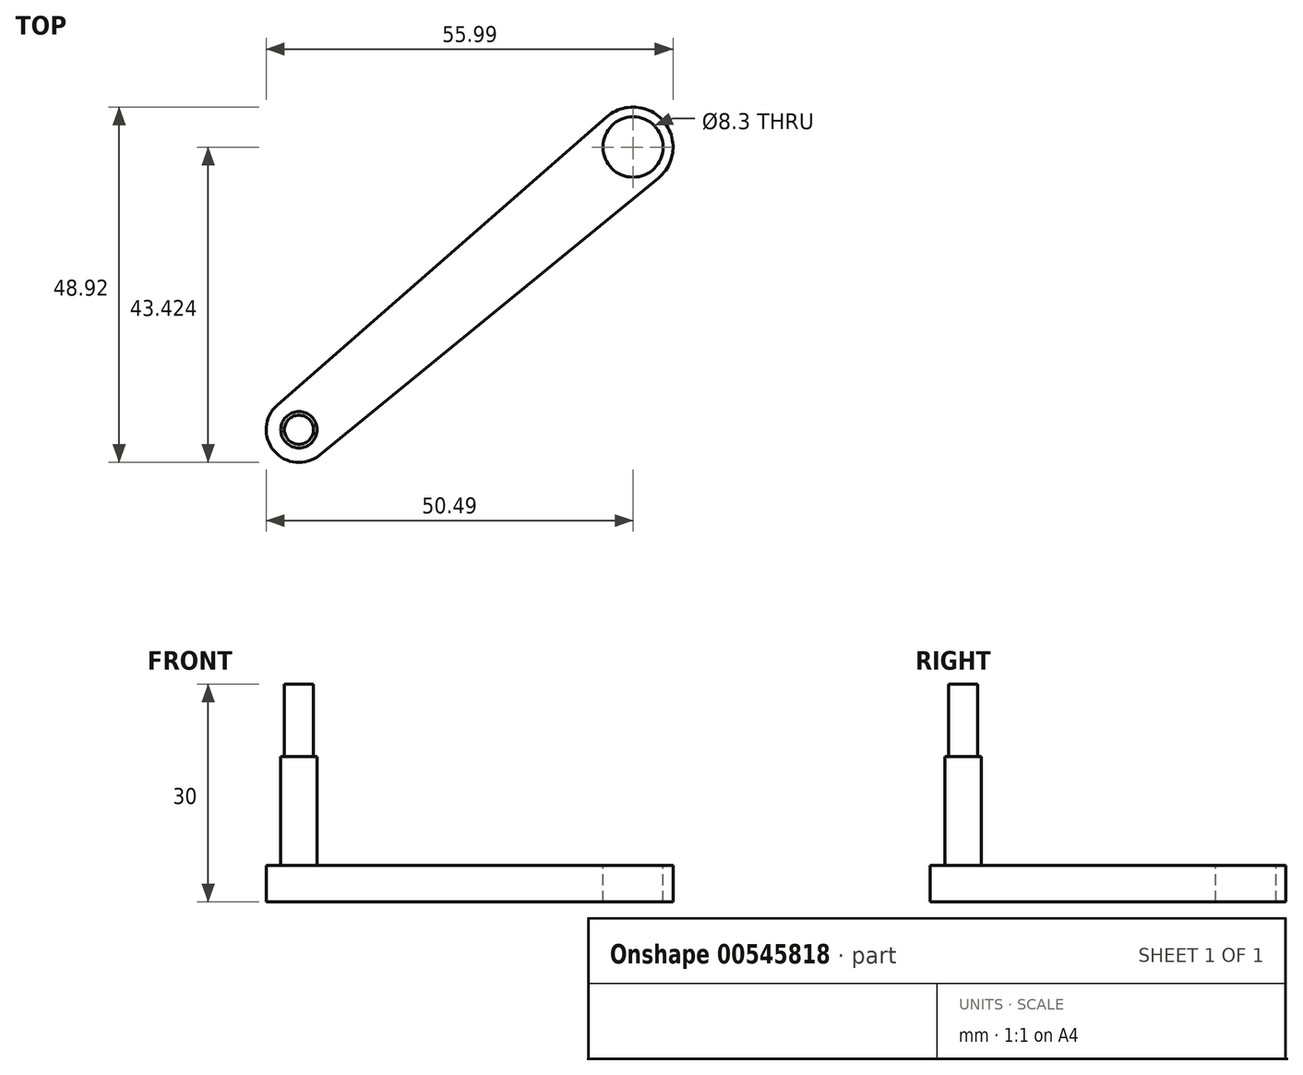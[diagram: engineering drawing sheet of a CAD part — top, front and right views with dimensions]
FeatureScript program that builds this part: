
annotation { "Feature Type Name" : "Feature", "Feature Type Description" : "" }
export const myFeature = defineFeature(function(context is Context, id is Id, definition is map)
    precondition{}
    {
        {
            var Q0;
            Q0=qCreatedBy(makeId("Top.planeOp"),FACE);
            var sketch = newSketch(context, id + "F0", { "sketchPlane" : qUnion([Q0])});
            skLineSegment(sketch, "E0.bottom", {"start": v(-70, 60) * mm, "end": v(70, 60) * mm});
            skLineSegment(sketch, "E0.top", {"start": v(-70, -60) * mm, "end": v(70, -60) * mm});
            skLineSegment(sketch, "E0.left", {"start": v(-70, 60) * mm, "end": v(-70, -60) * mm});
            skLineSegment(sketch, "E0.right", {"start": v(70, 60) * mm, "end": v(70, -60) * mm});
            skSolve(sketch);
        }
        {
            var Q0;
            Q0 = qSketchRegion(id + "F0", true);
            extrude(context, id + "F1", {"entities" : qUnion([Q0]), "depth" : 25 * mm, "offsetDistance" : 25 * mm});
        }
        {
            var Q0;
            Q0=makeQuery(id+"F1.opExtrude","CAP_FACE",FACE,{"disambiguationData":[OSD([sQuery(id+"F0.wireOp",EDGE,"E0.bottom"),sQuery(id+"F0.wireOp",EDGE,"E0.top"),sQuery(id+"F0.wireOp",EDGE,"E0.left"),sQuery(id+"F0.wireOp",EDGE,"E0.right")])],"isStart":false});
            var sketch = newSketch(context, id + "F2", { "sketchPlane" : qUnion([Q0])});
            skCircle(sketch, "E1", {"center": v(46.53, 42.76) * mm, "radius": 4.15 * mm});
            skSolve(sketch);
        }
        {
            var Q0;
            Q0 = qSketchRegion(id + "F2", true);
            extrude(context, id + "F3", {"entities" : qUnion([Q0]), "operationType" : NewBodyOperationType.REMOVE, "endBound" : BoundingType.THROUGH_ALL, "oppositeDirection" : true, "depth" : 25 * mm, "offsetDistance" : 25 * mm});
        }
        {
            var Q0;
            Q0=makeQuery(id+"F1.opExtrude","CAP_FACE",FACE,{"disambiguationData":[OSD([sQuery(id+"F0.wireOp",EDGE,"E0.bottom"),sQuery(id+"F0.wireOp",EDGE,"E0.top"),sQuery(id+"F0.wireOp",EDGE,"E0.left"),sQuery(id+"F0.wireOp",EDGE,"E0.right")])],"isStart":false});
            var sketch = newSketch(context, id + "F4", { "sketchPlane" : qUnion([Q0])});
            skCircle(sketch, "E2", {"center": v(0.54, 3.84) * mm, "radius": 2.5 * mm});
            skPoint(sketch, "E3.0.center.orphan", {"position": v(46.53, 42.76) * mm});
            skCircle(sketch, "E4.0", {"center": v(46.53, 42.76) * mm, "radius": 4.15 * mm, "construction": true});
            skSolve(sketch);
        }
        {
            var Q0;
            Q0 = qSketchRegion(id + "F4", true);
            extrude(context, id + "F5", {"entities" : qUnion([Q0]), "operationType" : NewBodyOperationType.ADD, "depth" : 25 * mm, "offsetDistance" : 25 * mm});
        }
        {
            var Q0;
            Q0=makeQuery(id+"F1.opExtrude","CAP_FACE",FACE,{"disambiguationData":[OSD([sQuery(id+"F0.wireOp",EDGE,"E0.bottom"),sQuery(id+"F0.wireOp",EDGE,"E0.top"),sQuery(id+"F0.wireOp",EDGE,"E0.left"),sQuery(id+"F0.wireOp",EDGE,"E0.right")])],"isStart":true});
            var sketch = newSketch(context, id + "F6", { "sketchPlane" : qUnion([Q0])});
            skArc(sketch, "E5", {"start": v(42.9, -46.9) * mm, "mid": v(50.73, -46.32) * mm, "end": v(50.01, -38.5) * mm});
            skCircle(sketch, "E6.0", {"center": v(0.54, -3.84) * mm, "radius": 2.5 * mm, "construction": true});
            skArc(sketch, "E7", {"start": v(3.39, -0.36) * mm, "mid": v(-2.9, -0.94) * mm, "end": v(-2.42, -7.23) * mm});
            skLineSegment(sketch, "E8", {"start": v(-2.42, -7.23) * mm, "end": v(42.9, -46.9) * mm});
            skLineSegment(sketch, "E9", {"start": v(50.01, -38.5) * mm, "end": v(3.39, -0.36) * mm});
            skSolve(sketch);
        }
        {
            var Q0;
            Q0 = qSketchRegion(id + "F6", true);
            extrude(context, id + "F7", {"entities" : qUnion([Q0]), "operationType" : NewBodyOperationType.INTERSECT, "endBound" : BoundingType.THROUGH_ALL, "oppositeDirection" : true, "depth" : 25 * mm, "offsetDistance" : 25 * mm});
        }
        {
            var Q0;
            Q0=makeQuery(id+"F1.opExtrude","CAP_FACE",FACE,{"disambiguationData":[OSD([sQuery(id+"F0.wireOp",EDGE,"E0.bottom"),sQuery(id+"F0.wireOp",EDGE,"E0.top"),sQuery(id+"F0.wireOp",EDGE,"E0.left"),sQuery(id+"F0.wireOp",EDGE,"E0.right")])],"isStart":true});
            var sketch = newSketch(context, id + "F8", { "sketchPlane" : qUnion([Q0])});
            skLineSegment(sketch, "E10.0", {"start": v(50.01, -38.5) * mm, "end": v(3.39, -0.36) * mm});
            skLineSegment(sketch, "E10.1", {"start": v(-2.42, -7.23) * mm, "end": v(42.9, -46.9) * mm});
            skArc(sketch, "E10.2", {"start": v(42.9, -46.9) * mm, "mid": v(50.73, -46.32) * mm, "end": v(50.01, -38.5) * mm});
            skArc(sketch, "E10.3", {"start": v(3.39, -0.36) * mm, "mid": v(-2.9, -0.94) * mm, "end": v(-2.42, -7.23) * mm});
            skSolve(sketch);
        }
        {
            var Q0;
            Q0 = qSketchRegion(id + "F8", true);
            extrude(context, id + "F9", {"entities" : qUnion([Q0]), "operationType" : NewBodyOperationType.REMOVE, "oppositeDirection" : true, "depth" : 20 * mm, "offsetDistance" : 25 * mm});
        }
        {
            var Q0;
            Q0=makeQuery(id+"F5.opExtrude","CAP_FACE",FACE,{"disambiguationData":[OSD([sQuery(id+"F4.wireOp",EDGE,"E2")])],"isStart":false});
            var sketch = newSketch(context, id + "F10", { "sketchPlane" : qUnion([Q0])});
            skCircle(sketch, "E11.0", {"center": v(0.54, 3.84) * mm, "radius": 2.5 * mm});
            skCircle(sketch, "E12", {"center": v(0.54, 3.84) * mm, "radius": 2 * mm});
            skSolve(sketch);
        }
        {
            var Q0;
            Q0 = qSketchRegion(id + "F10", true);
            extrude(context, id + "F11", {"entities" : qUnion([Q0]), "operationType" : NewBodyOperationType.REMOVE, "oppositeDirection" : true, "depth" : 10 * mm, "offsetDistance" : 25 * mm});
        }
    });
